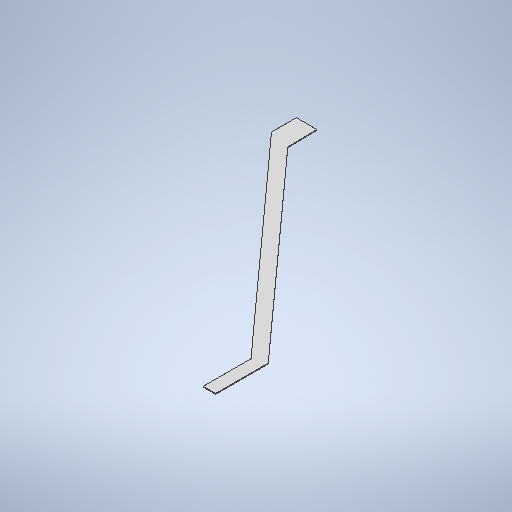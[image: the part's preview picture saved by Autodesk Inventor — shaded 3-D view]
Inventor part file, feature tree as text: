
AUTODESK INVENTOR PART (.ipt)
format: ipt  version: 2025 (Build 290162010, 162A)  size: 314,368 bytes
history: native  units: mm
features: sheet_metal_op x1, sketch x1, other x1
ambient origin geometry x8: Origin, YZ Plane, XZ Plane, XY Plane, X Axis, Y Axis, Z Axis, Center Point
bodies: Solid1 (feature_tree)
feature tree (3):
  sheet_metal_op  "Face1"
  sketch  "Sketch1"  dims[d2=3.0mm d3=2400.0mm d4=2950.0mm d5=50.0mm d6=100.0mm d7=50.0mm d9=135.0deg d10=950.0mm d11=1150.0mm d12=23.743743mm d13=50.0mm d14=100.0mm d15=212.132034mm d17=55.0mm d18=200.0mm d19=200.0mm d20=200.0mm d26=3.0mm d50=2705.0mm d53=50.0mm d55=1895.0mm d56=50.0mm d57=100.0mm d59=403.0mm d60=50.0mm d62=50.0mm d63=3.0mm d65=264.262262mm]
  other  "Plate1"
